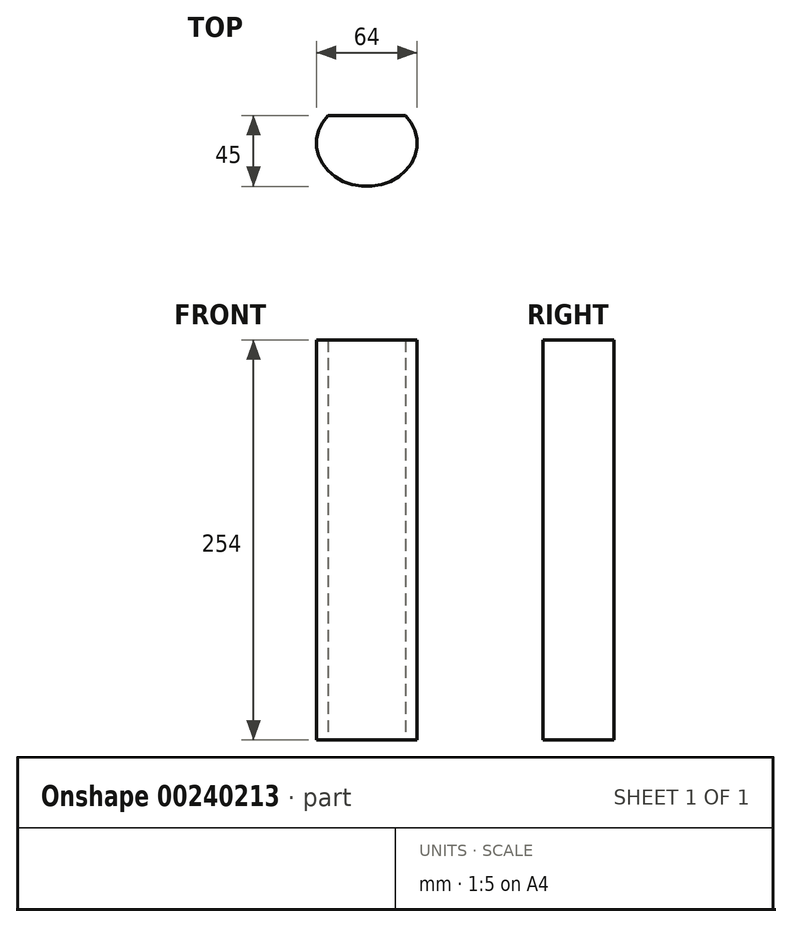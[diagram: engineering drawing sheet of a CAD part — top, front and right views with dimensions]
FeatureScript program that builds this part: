
annotation { "Feature Type Name" : "Feature", "Feature Type Description" : "" }
export const myFeature = defineFeature(function(context is Context, id is Id, definition is map)
    precondition{}
    {
        {
            var Q0;
            Q0=qCreatedBy(makeId("Top.planeOp"),FACE);
            var sketch = newSketch(context, id + "F0", { "sketchPlane" : qUnion([Q0])});
            skEllipticalArc(sketch, "E0", {});
            skLineSegment(sketch, "E1", {"start": v(-24.68, 17.5) * mm, "end": v(24.68, 17.5) * mm});
            skPoint(sketch, "E2.startSnap0", {"position": v(0, 27.5) * mm});
            skPoint(sketch, "E3.orphan", {"position": v(24.68, 27.5) * mm});
            skPoint(sketch, "E2.start.orphan", {"position": v(-24.68, 27.5) * mm});
            const initialGuessF0  = {"E0": [0, 0, 1, 0, 0.032, 0.0275, 2.4518176528042996, 0.6897750007854935]};
            skSetInitialGuess(sketch, initialGuessF0);
            skSolve(sketch);
        }
        {
            var Q0;
            Q0=makeQuery(id+"F0.imprint","IMPRINT",FACE,{"disambiguationData":[TD([[makeQuery(id+"F0.imprint","IMPRINT",EDGE,{"derivedFrom":sQuery(id+"F0.wireOp",EDGE,"E0")}),1.0]])]});
            extrude(context, id + "F1", {"entities" : qUnion([Q0]), "depth" : 254 * mm});
        }
    });
